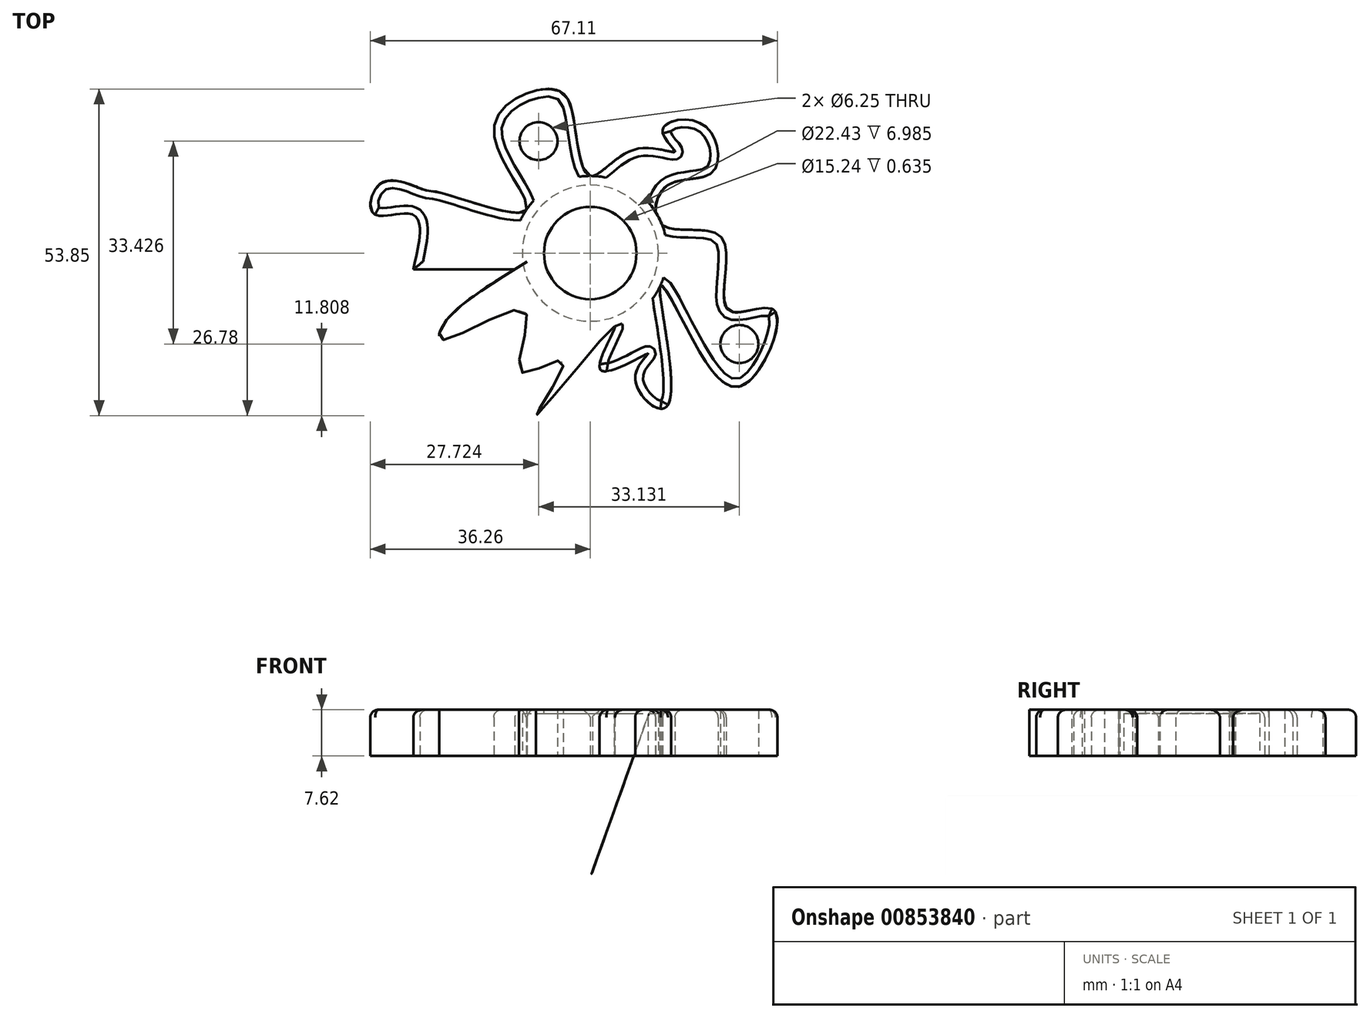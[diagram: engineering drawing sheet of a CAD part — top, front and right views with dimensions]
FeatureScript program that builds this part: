
annotation { "Feature Type Name" : "Feature", "Feature Type Description" : "" }
export const myFeature = defineFeature(function(context is Context, id is Id, definition is map)
    precondition{}
    {
        {
            var Q0;
            Q0=qCreatedBy(makeId("Top.planeOp"),FACE);
            var sketch = newSketch(context, id + "F0", { "sketchPlane" : qUnion([Q0])});
            skCircle(sketch, "E0", {"center": v(0, 0) * mm, "radius": 12.73 * mm});
            skLineSegment(sketch, "E1", {"start": v(-12.44, -2.67) * mm, "end": v(-29.18, -2.67) * mm});
            skFitSpline(sketch, "E2", {"points": [v(-29.18, -2.67) * mm, v(-29.18, 6.34) * mm, v(-35.72, 6.54) * mm, v(-34.3, 11.65) * mm, v(-27.34, 10.42) * mm, v(-24.89, 10.02) * mm, v(-10.58, 7.08) * mm, v(-15.9, 20.65) * mm, v(-5.88, 26.98) * mm, v(-2.6, 21.26) * mm, v(0, 12.73) * mm, v(7.62, 17.17) * mm, v(13.96, 16.76) * mm, v(11.91, 20.24) * mm, v(18.45, 21.26) * mm, v(20.3, 13.5) * mm, v(12.52, 11.04) * mm, v(11.84, 4.66) * mm, v(21.72, 2.45) * mm, v(22.75, -9.4) * mm, v(30.31, -9.4) * mm, v(25.4, -21.67) * mm, v(17.02, -14.52) * mm, v(11.48, -5.48) * mm, v(12.52, -25.35) * mm, v(7.41, -20.45) * mm, v(9.46, -16.56) * mm, v(1.69, -19.22) * mm, v(4.02, -12.07) * mm, v(-8.94, -26.78) * mm, v(-4.44, -17.79) * mm, v(-11.4, -19.63) * mm, v(-10.78, -9.61) * mm, v(-24.28, -14.31) * mm, v(-24.28, -11.86) * mm, v(-12.44, -2.67) * mm], "startDerivative": vector(98.03, 423.9) * mm, "endDerivative": vector(403.03, 249.83) * mm});
            skSolve(sketch);
        }
        {
            var Q0;
            Q0 = qSketchRegion(id + "F0", true);
            extrude(context, id + "F1", {"entities" : qUnion([Q0]), "depth" : 7.62 * mm, "offsetDistance" : 25.4 * mm});
        }
        {
            var Q0;
            Q0=makeQuery(id+"F1.opExtrude","CAP_FACE",FACE,{"disambiguationData":[OSD([sQuery(id+"F0.wireOp",EDGE,"E0"),sQuery(id+"F0.wireOp",EDGE,"E1"),sQuery(id+"F0.wireOp",EDGE,"E2")])],"isStart":true});
            var sketch = newSketch(context, id + "F2", { "sketchPlane" : qUnion([Q0])});
            skCircle(sketch, "E3", {"center": v(0, 0) * mm, "radius": 11.21 * mm});
            skSolve(sketch);
        }
        {
            var Q0;
            Q0 = qSketchRegion(id + "F2", true);
            extrude(context, id + "F3", {"entities" : qUnion([Q0]), "operationType" : NewBodyOperationType.REMOVE, "oppositeDirection" : true, "depth" : 7 * mm, "offsetDistance" : 25.4 * mm});
        }
        {
            var Q0;
            Q0=makeQuery(id+"F1.opExtrude","CAP_FACE",FACE,{"disambiguationData":[OSD([sQuery(id+"F0.wireOp",EDGE,"E0"),sQuery(id+"F0.wireOp",EDGE,"E1"),sQuery(id+"F0.wireOp",EDGE,"E2")])],"isStart":false});
            var sketch = newSketch(context, id + "F4", { "sketchPlane" : qUnion([Q0])});
            skCircle(sketch, "E4", {"center": v(0, 0) * mm, "radius": 7.62 * mm});
            skSolve(sketch);
        }
        {
            var Q0;
            Q0 = qSketchRegion(id + "F4", true);
            extrude(context, id + "F5", {"entities" : qUnion([Q0]), "operationType" : NewBodyOperationType.REMOVE, "oppositeDirection" : true, "depth" : 25.4 * mm, "offsetDistance" : 25.4 * mm});
        }
        {
            var Q0;
            Q0=makeQuery(id+"F1.opExtrude","CAP_FACE",FACE,{"disambiguationData":[OSD([sQuery(id+"F0.wireOp",EDGE,"E0"),sQuery(id+"F0.wireOp",EDGE,"E1"),sQuery(id+"F0.wireOp",EDGE,"E2")])],"isStart":true});
            var sketch = newSketch(context, id + "F6", { "sketchPlane" : qUnion([Q0])});
            skCircle(sketch, "E5", {"center": v(24.6, 14.97) * mm, "radius": 3.12 * mm});
            skCircle(sketch, "E6", {"center": v(-8.54, -18.45) * mm, "radius": 3.12 * mm});
            skSolve(sketch);
        }
        {
            var Q0;
            Q0 = qSketchRegion(id + "F6", true);
            extrude(context, id + "F7", {"entities" : qUnion([Q0]), "operationType" : NewBodyOperationType.REMOVE, "oppositeDirection" : true, "depth" : 25.4 * mm, "offsetDistance" : 25.4 * mm});
        }
        {
            var Q0;
            {var subQ0=sQuery(id+"F0.wireOp",EDGE,"E2");var subQ1=sQuery(id+"F0.wireOp",EDGE,"E0");Q0=makeQuery(id+"F1.opExtrude","CAP_EDGE",EDGE,{"disambiguationData":[OSD([subQ0]),TDD([makeQuery(id+"F0.imprint","IMPRINT",EDGE,{"disambiguationData":[TD([[makeQuery(id+"F0.imprint","INTERSECT",VERTEX,{"disambiguationData":[OD(7.0)],"derivedFrom":[subQ1,subQ0]}),1.0]])],"derivedFrom":subQ0})])],"isStart":false});}
            var Q1;
            {var subQ0=sQuery(id+"F0.wireOp",EDGE,"E2");var subQ1=sQuery(id+"F0.wireOp",EDGE,"E0");Q1=makeQuery(id+"F1.opExtrude","CAP_EDGE",EDGE,{"disambiguationData":[OSD([subQ0]),TDD([makeQuery(id+"F0.imprint","IMPRINT",EDGE,{"disambiguationData":[TD([[makeQuery(id+"F0.imprint","INTERSECT",VERTEX,{"disambiguationData":[OD(1.0)],"derivedFrom":[subQ1,subQ0]}),-1.0]])],"derivedFrom":subQ0})])],"isStart":false});}
            var Q2;
            {var subQ0=sQuery(id+"F0.wireOp",EDGE,"E2");var subQ1=sQuery(id+"F0.wireOp",EDGE,"E0");Q2=makeQuery(id+"F1.opExtrude","CAP_EDGE",EDGE,{"disambiguationData":[OSD([subQ0]),TDD([makeQuery(id+"F0.imprint","IMPRINT",EDGE,{"disambiguationData":[TD([[makeQuery(id+"F0.imprint","INTERSECT",VERTEX,{"disambiguationData":[OD(0.0)],"derivedFrom":[subQ1,subQ0]}),1.0]])],"derivedFrom":subQ0})])],"isStart":false});}
            var Q3;
            {var subQ0=sQuery(id+"F0.wireOp",EDGE,"E2");var subQ1=sQuery(id+"F0.wireOp",EDGE,"E0");Q3=makeQuery(id+"F1.opExtrude","CAP_EDGE",EDGE,{"disambiguationData":[OSD([subQ0]),TDD([makeQuery(id+"F0.imprint","IMPRINT",EDGE,{"disambiguationData":[TD([[makeQuery(id+"F0.imprint","INTERSECT",VERTEX,{"disambiguationData":[OD(3.0)],"derivedFrom":[subQ1,subQ0]}),1.0]])],"derivedFrom":subQ0})])],"isStart":false});}
            var Q4;
            {var subQ0=sQuery(id+"F0.wireOp",EDGE,"E2");Q4=makeQuery(id+"F1.opExtrude","CAP_EDGE",EDGE,{"disambiguationData":[OSD([subQ0]),TDD([makeQuery(id+"F0.imprint","IMPRINT",EDGE,{"disambiguationData":[TD([[makeQuery(id+"F0.imprint","INTERSECT",VERTEX,{"derivedFrom":[sQuery(id+"F0.wireOp",EDGE,"E1"),subQ0]}),-1.0]])],"derivedFrom":subQ0})])],"isStart":false});}
            var Q5;
            Q5=makeQuery(id+"F1.opExtrude","CAP_EDGE",EDGE,{"disambiguationData":[OSD([sQuery(id+"F0.wireOp",EDGE,"E1")])],"isStart":false});
            fillet(context, id + "F8", {"entities" : qUnion([Q0, Q1, Q2, Q3, Q4, Q5]), "radius" : 1.27 * mm, "tangentPropagation" : true, "allowEdgeOverflow" : false});
        }
    });
